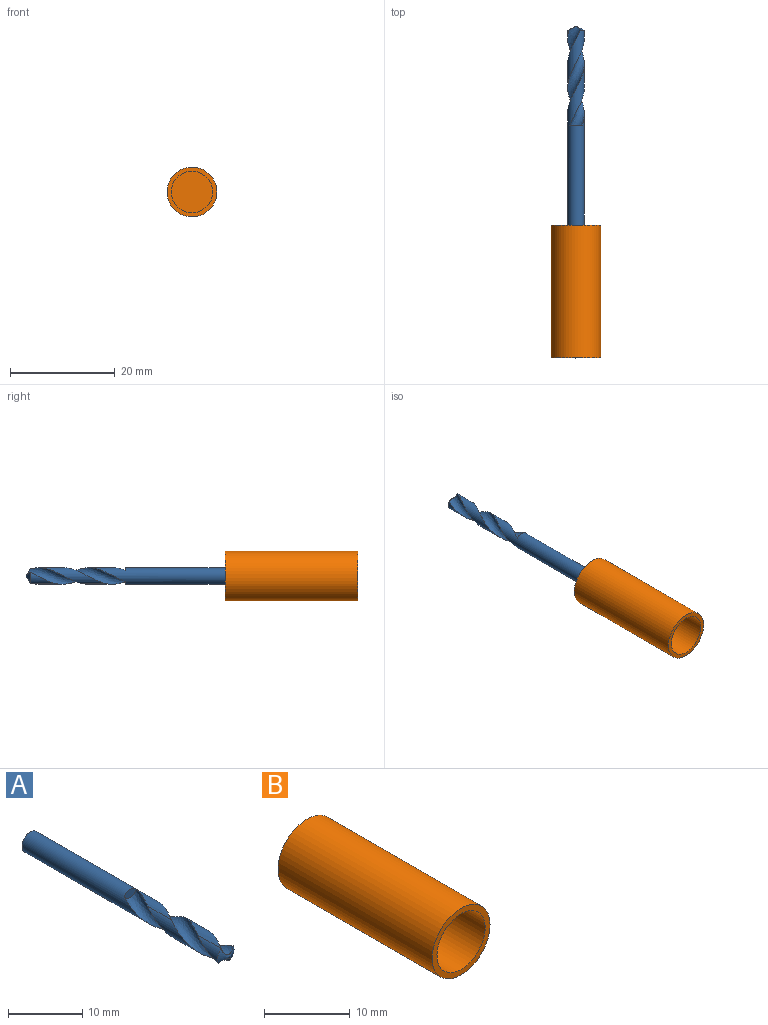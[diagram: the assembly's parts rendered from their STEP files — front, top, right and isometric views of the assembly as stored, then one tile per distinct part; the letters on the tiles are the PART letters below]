
ASSEMBLY  parts=2 mates=1
PART A: 9 faces, bbox 3.4x38.2x3.5 mm
  f0: cylinder r=1.59mm len=37.25mm, axis (0,1,0), area 243.1mm2, adj f1,f2,f3,f4,f6,f7,f8
  f1: cylinder r=1.59mm len=14.07mm, axis (0,1,0), area 28mm2, adj f0,f3,f4,f5
  f2: cylinder r=1.59mm len=4.54mm, axis (0,1,0), area 5.4mm2, adj f0,f4,f5
  f3: bspline ~19.05x3.31mm, area 57.1mm2, adj f0,f1,f5,f7
  f4: bspline ~19.05x3.31mm, area 56mm2, adj f0,f1,f2,f5,f6
  f5: cone r=0mm half-angle=63.1deg, axis (0,1,0), area 4.2mm2, adj f1,f2,f3,f4
  f6: plane 2.46x1.41mm, normal (0,-1,0), area 2.1mm2, adj f0,f4
  f7: plane 2.46x1.41mm, normal (0,-1,0), area 2.1mm2, adj f0,f3
  f8: plane 3.18x3.18mm, normal (0,1,0), area 7.9mm2, adj f0
PART B: 5 faces, bbox 9.5x25.4x9.5 mm
  f0: cylinder r=4.76mm len=25.4mm, axis (0,1,0), area 760.1mm2, adj f1,f2
  f1: plane 9.53x9.53mm, normal (0,-1,0), area 21.8mm2, adj f0,f3
  f2: plane 9.53x9.53mm, normal (0,1,0), area 71.3mm2, adj f0
  f3: cylinder r=3.97mm len=19.84mm, axis (0,1,0), area 494.8mm2, adj f1,f4
  f4: plane 7.94x7.94mm, normal (0,-1,0), area 49.5mm2, adj f3
PLACE A rot(axis=(1,0,0),180deg) t=(-9.22,22.32,-6.15)mm
PLACE B t=(-9.22,3.27,-6.15)mm
MATE cylindrical A.f0 <-> B.f0  axis (0,-1,0) through (-9.22,3.27,-6.15)mm
